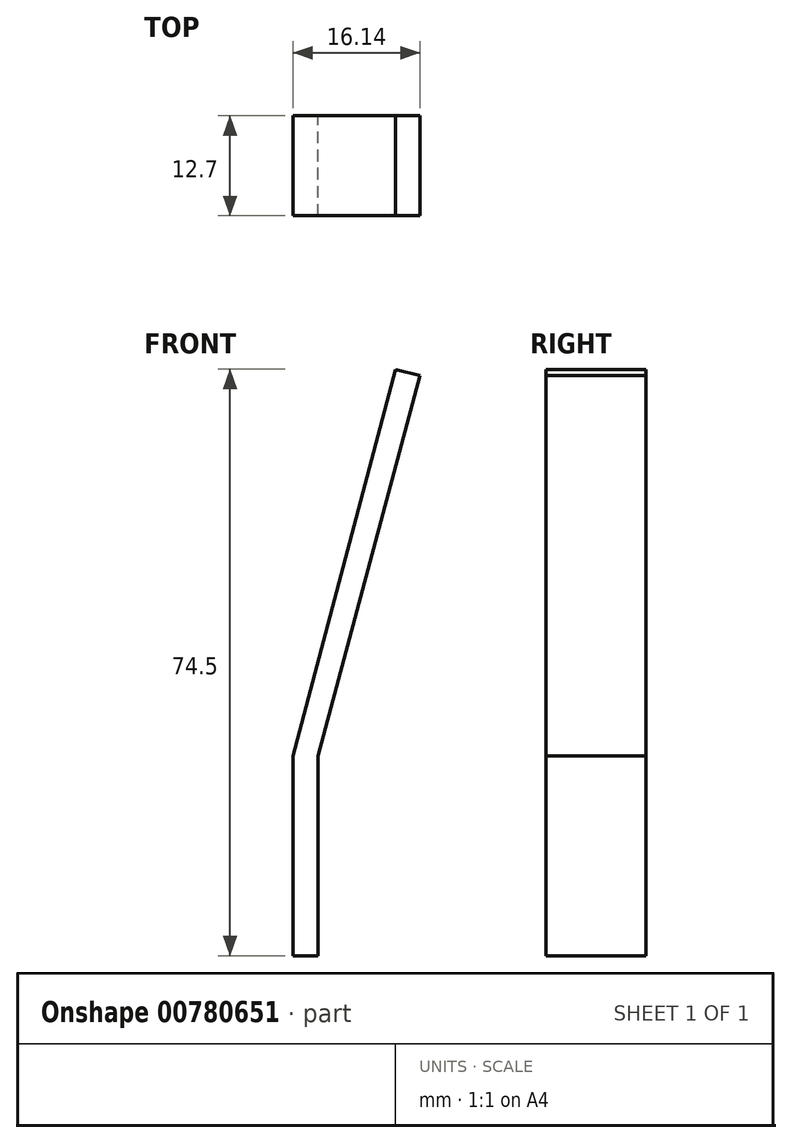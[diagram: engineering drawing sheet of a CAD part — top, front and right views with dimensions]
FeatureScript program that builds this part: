
annotation { "Feature Type Name" : "Feature", "Feature Type Description" : "" }
export const myFeature = defineFeature(function(context is Context, id is Id, definition is map)
    precondition{}
    {
        {
            var Q0;
            Q0=qCreatedBy(makeId("Front.planeOp"),FACE);
            var sketch = newSketch(context, id + "F0", { "sketchPlane" : qUnion([Q0])});
            skLineSegment(sketch, "E0", {"start": v(0, 0) * mm, "end": v(0, -25.4) * mm});
            skLineSegment(sketch, "E1", {"start": v(0, -25.4) * mm, "end": v(-3.2, -25.4) * mm});
            skLineSegment(sketch, "E2", {"start": v(-3.2, -25.4) * mm, "end": v(-3.2, 0) * mm});
            skLineSegment(sketch, "E3", {"start": v(-3.2, 0) * mm, "end": v(9.84, 49.1) * mm});
            skLineSegment(sketch, "E4", {"start": v(9.84, 49.1) * mm, "end": v(12.94, 48.28) * mm});
            skLineSegment(sketch, "E5", {"start": v(12.94, 48.28) * mm, "end": v(0, 0) * mm});
            skSolve(sketch);
        }
        {
            var Q0;
            Q0 = qSketchRegion(id + "F0", true);
            extrude(context, id + "F1", {"entities" : qUnion([Q0]), "endBound" : BoundingType.SYMMETRIC, "depth" : 12.7 * mm, "offsetDistance" : 25 * mm});
        }
    });
